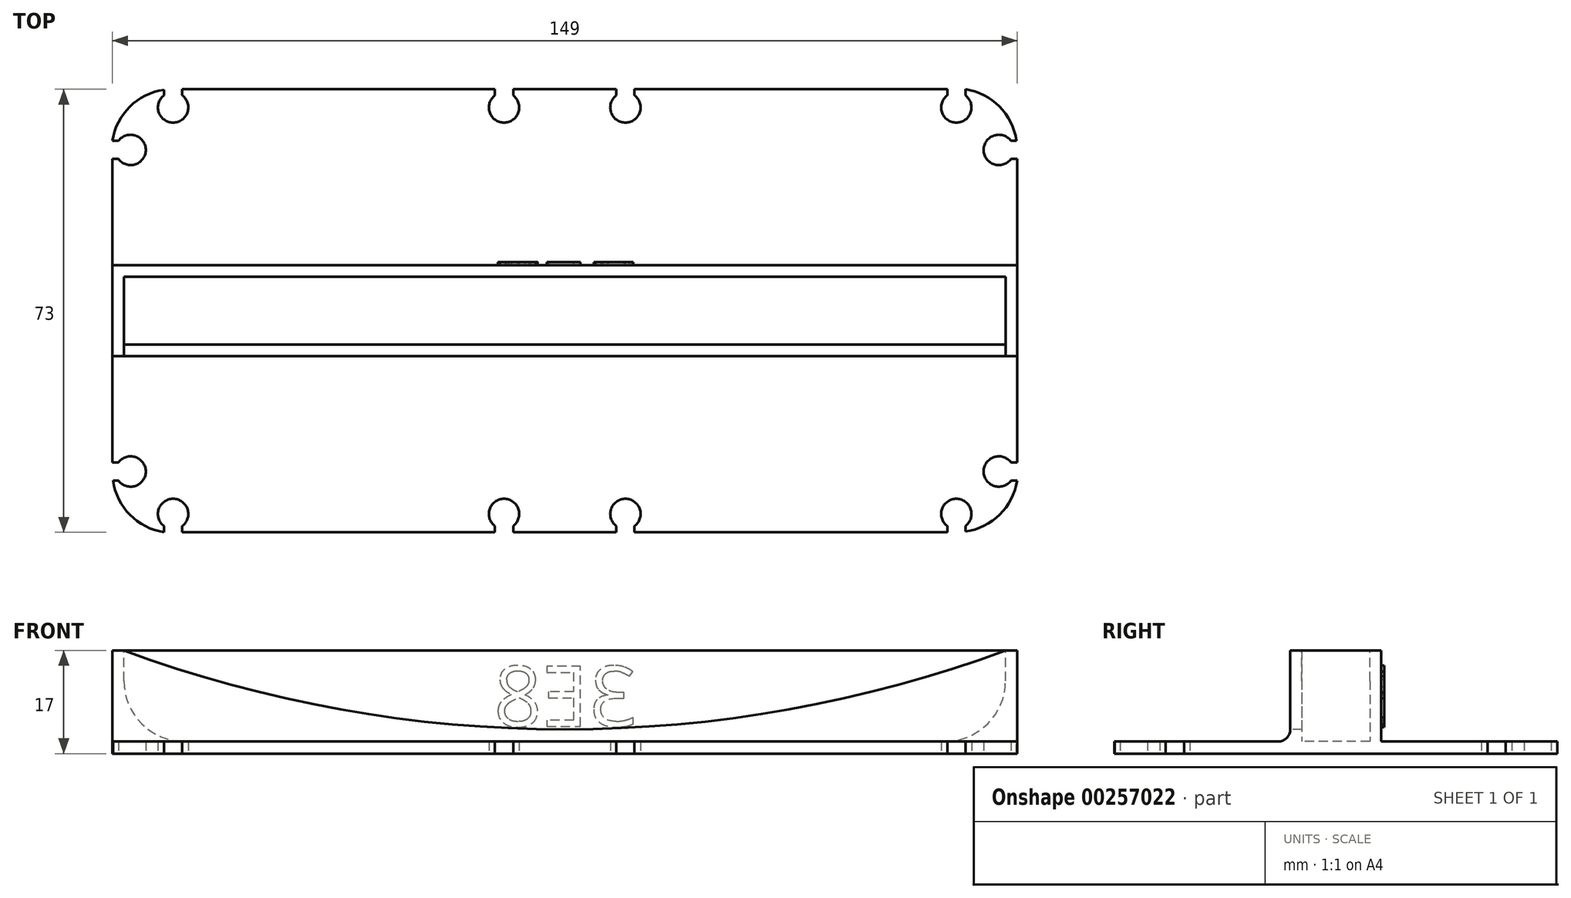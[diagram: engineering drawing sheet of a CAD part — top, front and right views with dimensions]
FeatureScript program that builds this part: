
annotation { "Feature Type Name" : "Feature", "Feature Type Description" : "" }
export const myFeature = defineFeature(function(context is Context, id is Id, definition is map)
    precondition{}
    {
        {
            var Q0;
            Q0=qCreatedBy(makeId("Top.planeOp"),FACE);
            var sketch = newSketch(context, id + "F0", { "sketchPlane" : qUnion([Q0])});
            skLineSegment(sketch, "E0.bottom", {"start": v(74.5, -36.5) * mm, "end": v(-74.5, -36.5) * mm});
            skLineSegment(sketch, "E0.top", {"start": v(74.5, 36.5) * mm, "end": v(-74.5, 36.5) * mm});
            skLineSegment(sketch, "E0.left", {"start": v(74.5, -36.5) * mm, "end": v(74.5, 36.5) * mm});
            skLineSegment(sketch, "E0.right", {"start": v(-74.5, -36.5) * mm, "end": v(-74.5, 36.5) * mm});
            skPoint(sketch, "E0.middle", {"position": v(0, 0) * mm});
            skLineSegment(sketch, "E1", {"start": v(0, 0) * mm, "end": v(0, 36.5) * mm, "construction": true});
            skLineSegment(sketch, "E2", {"start": v(0, 0) * mm, "end": v(-74.5, 0) * mm, "construction": true});
            skLineSegment(sketch, "E3", {"start": v(-74.5, -36.5) * mm, "end": v(-64.5, -36.5) * mm, "construction": true});
            skLineSegment(sketch, "E4", {"start": v(-66, -36.5) * mm, "end": v(-66, -35.5) * mm});
            skLineSegment(sketch, "E5", {"start": v(-66, -35.5) * mm, "end": v(-63, -35.5) * mm, "construction": true});
            skLineSegment(sketch, "E6", {"start": v(-63, -35.5) * mm, "end": v(-63, -36.5) * mm});
            skLineSegment(sketch, "E7", {"start": v(-64.5, -36.5) * mm, "end": v(-64.5, -35.5) * mm, "construction": true});
            skArc(sketch, "E8", {"start": v(-63, -35.5) * mm, "mid": v(-64.5, -31) * mm, "end": v(-66, -35.5) * mm});
            skLineSegment(sketch, "E9", {"start": v(-74.5, -36.5) * mm, "end": v(-59.3, -21.3) * mm, "construction": true});
            skArc(sketch, "E10.MirrorCS", {"start": v(-73.5, -25) * mm, "mid": v(-69, -26.5) * mm, "end": v(-73.5, -28) * mm});
            skLineSegment(sketch, "E11.MirrorCS", {"start": v(-74.5, -28) * mm, "end": v(-73.5, -28) * mm});
            skLineSegment(sketch, "E12.MirrorCS", {"start": v(-73.5, -25) * mm, "end": v(-74.5, -25) * mm});
            skLineSegment(sketch, "E13.MirrorCS", {"start": v(-73.5, 25) * mm, "end": v(-74.5, 25) * mm});
            skArc(sketch, "E14.MirrorCS", {"start": v(-73.5, 25) * mm, "mid": v(-69, 26.5) * mm, "end": v(-73.5, 28) * mm});
            skLineSegment(sketch, "E15.MirrorCS", {"start": v(-74.5, 28) * mm, "end": v(-73.5, 28) * mm});
            skLineSegment(sketch, "E16.MirrorCS", {"start": v(-66, 36.5) * mm, "end": v(-66, 35.5) * mm});
            skArc(sketch, "E17.MirrorCS", {"start": v(-63, 35.5) * mm, "mid": v(-64.5, 31) * mm, "end": v(-66, 35.5) * mm});
            skLineSegment(sketch, "E18.MirrorCS", {"start": v(-63, 35.5) * mm, "end": v(-63, 36.5) * mm});
            skArc(sketch, "E19.MirrorCS", {"start": v(63, 35.5) * mm, "mid": v(64.5, 31) * mm, "end": v(66, 35.5) * mm});
            skLineSegment(sketch, "E20.MirrorCS", {"start": v(63, 35.5) * mm, "end": v(63, 36.5) * mm});
            skLineSegment(sketch, "E21.MirrorCS", {"start": v(66, 36.5) * mm, "end": v(66, 35.5) * mm});
            skArc(sketch, "E22.MirrorCS", {"start": v(73.5, 25) * mm, "mid": v(69, 26.5) * mm, "end": v(73.5, 28) * mm});
            skLineSegment(sketch, "E23.MirrorCS", {"start": v(74.5, 28) * mm, "end": v(73.5, 28) * mm});
            skLineSegment(sketch, "E24.MirrorCS", {"start": v(73.5, 25) * mm, "end": v(74.5, 25) * mm});
            skLineSegment(sketch, "E25.MirrorCS", {"start": v(63, -35.5) * mm, "end": v(63, -36.5) * mm});
            skArc(sketch, "E26.MirrorCS", {"start": v(63, -35.5) * mm, "mid": v(64.5, -31) * mm, "end": v(66, -35.5) * mm});
            skLineSegment(sketch, "E27.MirrorCS", {"start": v(66, -36.5) * mm, "end": v(66, -35.5) * mm});
            skLineSegment(sketch, "E28.MirrorCS", {"start": v(74.5, -28) * mm, "end": v(73.5, -28) * mm});
            skArc(sketch, "E29.MirrorCS", {"start": v(73.5, -25) * mm, "mid": v(69, -26.5) * mm, "end": v(73.5, -28) * mm});
            skLineSegment(sketch, "E30.MirrorCS", {"start": v(73.5, -25) * mm, "end": v(74.5, -25) * mm});
            skLineSegment(sketch, "E31", {"start": v(-37.25, 0) * mm, "end": v(-37.25, -36.5) * mm, "construction": true});
            skLineSegment(sketch, "E32.MirrorCS", {"start": v(-11.5, -35.5) * mm, "end": v(-11.5, -36.5) * mm});
            skArc(sketch, "E33.MirrorCS", {"start": v(-11.5, -35.5) * mm, "mid": v(-10, -31) * mm, "end": v(-8.5, -35.5) * mm});
            skLineSegment(sketch, "E34.MirrorCS", {"start": v(-8.5, -36.5) * mm, "end": v(-8.5, -35.5) * mm});
            skLineSegment(sketch, "E35.MirrorCS", {"start": v(-8.5, 36.5) * mm, "end": v(-8.5, 35.5) * mm});
            skArc(sketch, "E36.MirrorCS", {"start": v(-11.5, 35.5) * mm, "mid": v(-10, 31) * mm, "end": v(-8.5, 35.5) * mm});
            skLineSegment(sketch, "E37.MirrorCS", {"start": v(-11.5, 35.5) * mm, "end": v(-11.5, 36.5) * mm});
            skLineSegment(sketch, "E38.MirrorCS", {"start": v(11.5, 35.5) * mm, "end": v(11.5, 36.5) * mm});
            skArc(sketch, "E39.MirrorCS", {"start": v(11.5, 35.5) * mm, "mid": v(10, 31) * mm, "end": v(8.5, 35.5) * mm});
            skLineSegment(sketch, "E40.MirrorCS", {"start": v(8.5, 36.5) * mm, "end": v(8.5, 35.5) * mm});
            skLineSegment(sketch, "E41.MirrorCS", {"start": v(8.5, -36.5) * mm, "end": v(8.5, -35.5) * mm});
            skArc(sketch, "E42.MirrorCS", {"start": v(11.5, -35.5) * mm, "mid": v(10, -31) * mm, "end": v(8.5, -35.5) * mm});
            skLineSegment(sketch, "E43.MirrorCS", {"start": v(11.5, -35.5) * mm, "end": v(11.5, -36.5) * mm});
            skSolve(sketch);
        }
        {
            var Q0;
            {var subQ4=sQuery(id+"F0.wireOp",EDGE,"E4");Q0=makeQuery(id+"F0.imprint","IMPRINT",FACE,{"disambiguationData":[TD([[makeQuery(id+"F0.imprint","IMPRINT",EDGE,{"derivedFrom":subQ4}),1.0]])]});}
            extrude(context, id + "F1", {"entities" : qUnion([Q0]), "depth" : 2 * mm});
        }
        {
            var Q0;
            Q0=makeQuery(id+"F1.opExtrude","CAP_FACE",FACE,{"disambiguationData":[OSD([sQuery(id+"F0.wireOp",EDGE,"E0.bottom"),sQuery(id+"F0.wireOp",EDGE,"E0.top"),sQuery(id+"F0.wireOp",EDGE,"E0.left"),sQuery(id+"F0.wireOp",EDGE,"E0.right")])],"isStart":false});
            var sketch = newSketch(context, id + "F2", { "sketchPlane" : qUnion([Q0])});
            skLineSegment(sketch, "E44.bottom", {"start": v(74.5, -7.5) * mm, "end": v(-74.5, -7.5) * mm});
            skLineSegment(sketch, "E44.top", {"start": v(74.5, 7.5) * mm, "end": v(-74.5, 7.5) * mm});
            skLineSegment(sketch, "E44.left", {"start": v(74.5, -7.5) * mm, "end": v(74.5, 7.5) * mm});
            skLineSegment(sketch, "E44.right", {"start": v(-74.5, -7.5) * mm, "end": v(-74.5, 7.5) * mm});
            skPoint(sketch, "E44.middle", {"position": v(0, 0) * mm});
            skSolve(sketch);
        }
        {
            var Q0;
            Q0 = qSketchRegion(id + "F2", true);
            extrude(context, id + "F3", {"entities" : qUnion([Q0]), "operationType" : NewBodyOperationType.ADD, "depth" : 15 * mm});
        }
        {
            var Q0;
            Q0=makeQuery(id+"F3.opExtrude","CAP_FACE",FACE,{"disambiguationData":[OSD([sQuery(id+"F2.wireOp",EDGE,"E44.bottom"),sQuery(id+"F2.wireOp",EDGE,"E44.top"),sQuery(id+"F2.wireOp",EDGE,"E44.left"),sQuery(id+"F2.wireOp",EDGE,"E44.right")])],"isStart":false});
            var sketch = newSketch(context, id + "F4", { "sketchPlane" : qUnion([Q0])});
            skLineSegment(sketch, "E45.bottom", {"start": v(72.6, -5.6) * mm, "end": v(-72.6, -5.6) * mm});
            skLineSegment(sketch, "E45.top", {"start": v(72.6, 5.6) * mm, "end": v(-72.6, 5.6) * mm});
            skLineSegment(sketch, "E45.left", {"start": v(72.6, -5.6) * mm, "end": v(72.6, 5.6) * mm});
            skLineSegment(sketch, "E45.right", {"start": v(-72.6, -5.6) * mm, "end": v(-72.6, 5.6) * mm});
            skPoint(sketch, "E45.middle", {"position": v(0, 0) * mm});
            skLineSegment(sketch, "E46", {"start": v(0, 5.6) * mm, "end": v(0, 7.5) * mm, "construction": true});
            skLineSegment(sketch, "E47", {"start": v(-72.6, 0) * mm, "end": v(-74.5, 0) * mm, "construction": true});
            skSolve(sketch);
        }
        {
            var Q0;
            Q0 = qSketchRegion(id + "F4", true);
            var Q1;
            {var subQ0=sQuery(id+"F0.wireOp",EDGE,"E0.right");var subQ1=sQuery(id+"F0.wireOp",EDGE,"E0.left");var subQ2=sQuery(id+"F0.wireOp",EDGE,"E0.bottom");Q1=makeQuery(id+"F3.boolean.opBoolean","SPLIT",FACE,{"disambiguationData":[TD([makeQuery(id+"F1.opExtrude","SWEPT_FACE",FACE,{"disambiguationData":[OSD([subQ2])]})])],"derivedFrom":makeQuery(id+"F1.opExtrude","CAP_FACE",FACE,{"disambiguationData":[OSD([subQ2,sQuery(id+"F0.wireOp",EDGE,"E0.top"),subQ1,subQ0])],"isStart":false})});}
            extrude(context, id + "F5", {"entities" : qUnion([Q0]), "operationType" : NewBodyOperationType.REMOVE, "endBound" : BoundingType.UP_TO_SURFACE, "oppositeDirection" : true, "endBoundEntityFace" : qUnion([Q1]), "depth" : 25 * mm});
        }
        {
            var Q0;
            Q0=makeQuery(id+"F3.opExtrude","SWEPT_FACE",FACE,{"disambiguationData":[OSD([sQuery(id+"F2.wireOp",EDGE,"E44.bottom")])]});
            var sketch = newSketch(context, id + "F6", { "sketchPlane" : qUnion([Q0])});
            skPoint(sketch, "E48.0", {"position": v(-72.6, 17) * mm});
            skPoint(sketch, "E49.0", {"position": v(72.6, 17) * mm});
            skArc(sketch, "E50", {"start": v(-72.6, 17) * mm, "mid": v(0, 4) * mm, "end": v(72.6, 17) * mm});
            skLineSegment(sketch, "E51", {"start": v(0, 4) * mm, "end": v(0, 2) * mm, "construction": true});
            skLineSegment(sketch, "E52", {"start": v(-72.6, 17) * mm, "end": v(72.6, 17) * mm});
            skSolve(sketch);
        }
        {
            var Q0;
            Q0 = qSketchRegion(id + "F6", true);
            var Q1;
            Q1=makeQuery(id+"F5.boolean.opBoolean","COPY",FACE,{"derivedFrom":makeQuery(id+"F5.opExtrude","SWEPT_FACE",FACE,{"disambiguationData":[OSD([sQuery(id+"F4.wireOp",EDGE,"E45.top")])]})});
            extrude(context, id + "F7", {"entities" : qUnion([Q0]), "operationType" : NewBodyOperationType.REMOVE, "endBound" : BoundingType.UP_TO_SURFACE, "oppositeDirection" : true, "endBoundEntityFace" : qUnion([Q1]), "depth" : 25 * mm});
        }
        {
            var Q0;
            Q0=makeQuery(id+"F3.opExtrude","SWEPT_FACE",FACE,{"disambiguationData":[OSD([sQuery(id+"F2.wireOp",EDGE,"E44.top")])]});
            var sketch = newSketch(context, id + "F8", { "sketchPlane" : qUnion([Q0])});
            skLineSegment(sketch, "E53", {"start": v(0, 17) * mm, "end": v(0, 2) * mm, "construction": true});
            skText(sketch, "E54", { "text": "3E8", "fontName": "OpenSans-Regular.ttf"});
            skPoint(sketch, "E55", {"position": v(0, 9.5) * mm});
            const initialGuessF8  = {"E54": [-0.0119, 0.0045, 1, 0, 0.01]};
            skSetInitialGuess(sketch, initialGuessF8);
            skSolve(sketch);
        }
        {
            var Q0;
            Q0 = qSketchRegion(id + "F8", true);
            extrude(context, id + "F9", {"entities" : qUnion([Q0]), "operationType" : NewBodyOperationType.ADD, "depth" : .5 * mm});
        }
        {
            var Q0;
            Q0=makeQuery(id+"F3.opExtrude","CAP_EDGE",EDGE,{"disambiguationData":[OSD([sQuery(id+"F2.wireOp",EDGE,"E44.bottom")])],"isStart":true});
            var Q1;
            Q1=makeQuery(id+"F3.opExtrude","CAP_EDGE",EDGE,{"disambiguationData":[OSD([sQuery(id+"F2.wireOp",EDGE,"E44.top")])],"isStart":true});
            fillet(context, id + "F10", {"entities" : qUnion([Q0, Q1]), "radius" : 2 * mm, "tangentPropagation" : true, "allowEdgeOverflow" : false});
        }
        {
            var Q0;
            Q0=makeQuery(id+"F5.boolean.opBoolean","COPY",EDGE,{"derivedFrom":makeQuery(id+"F5.opExtrude","CAP_EDGE",EDGE,{"disambiguationData":[OSD([sQuery(id+"F4.wireOp",EDGE,"E45.right")])],"isStart":false})});
            var Q1;
            Q1=makeQuery(id+"F5.boolean.opBoolean","COPY",EDGE,{"derivedFrom":makeQuery(id+"F5.opExtrude","CAP_EDGE",EDGE,{"disambiguationData":[OSD([sQuery(id+"F4.wireOp",EDGE,"E45.left")])],"isStart":false})});
            var Q2;
            Q2=makeQuery(id+"F1.opExtrude","SWEPT_EDGE",EDGE,{"disambiguationData":[OSD([sQuery(id+"F0.wireOp",EDGE,"E0.bottom"),sQuery(id+"F0.wireOp",EDGE,"E0.left")])]});
            var Q3;
            Q3=makeQuery(id+"F1.opExtrude","SWEPT_EDGE",EDGE,{"disambiguationData":[OSD([sQuery(id+"F0.wireOp",EDGE,"E0.top"),sQuery(id+"F0.wireOp",EDGE,"E0.left")])]});
            var Q4;
            Q4=makeQuery(id+"F1.opExtrude","SWEPT_EDGE",EDGE,{"disambiguationData":[OSD([sQuery(id+"F0.wireOp",EDGE,"E0.bottom"),sQuery(id+"F0.wireOp",EDGE,"E0.right")])]});
            var Q5;
            Q5=makeQuery(id+"F1.opExtrude","SWEPT_EDGE",EDGE,{"disambiguationData":[OSD([sQuery(id+"F0.wireOp",EDGE,"E0.top"),sQuery(id+"F0.wireOp",EDGE,"E0.right")])]});
            var Q6;
            Q6=makeQuery(id+"FLN3ONRAx0sLFhP_1.opExtrude","CAP_EDGE",EDGE,{"disambiguationData":[OSD([sQuery(id+"F5YktYefHDFv0fp_1.wireOp",EDGE,"H54qWbda-DKNh-fhWI-mdyw-DauYGH6vxysM")])],"isStart":true});
            var Q7;
            {var subQ0=sQuery(id+"F4.wireOp",EDGE,"E45.left");Q7=makeQuery(id+"FLN3ONRAx0sLFhP_1.opExtrude","TWEAK_EDGE",EDGE,{"derivedFrom":[makeQuery(id+"F2G9z2ryyHDEi2k_1.boolean.opBoolean","MERGE",FACE,{"derivedFrom":[makeQuery(id+"F5.boolean.opBoolean","COPY",FACE,{"derivedFrom":makeQuery(id+"F5.opExtrude","SWEPT_FACE",FACE,{"disambiguationData":[OSD([subQ0])]})}),makeQuery(id+"F2G9z2ryyHDEi2k_1.opExtrude","CAP_FACE",FACE,{"disambiguationData":[OSD([subQ0])],"isStart":false})]}),makeQuery(id+"F5YktYefHDFv0fp_1.imprint","IMPRINT",EDGE,{"derivedFrom":sQuery(id+"F5YktYefHDFv0fp_1.wireOp",EDGE,"H54qWbda-DKNh-fhWI-mdyw-DauYGH6vxysM")})]});}
            fillet(context, id + "F11", {"entities" : qUnion([Q0, Q1, Q2, Q3, Q4, Q5, Q6, Q7]), "radius" : 10 * mm, "tangentPropagation" : true, "allowEdgeOverflow" : false});
        }
    });
